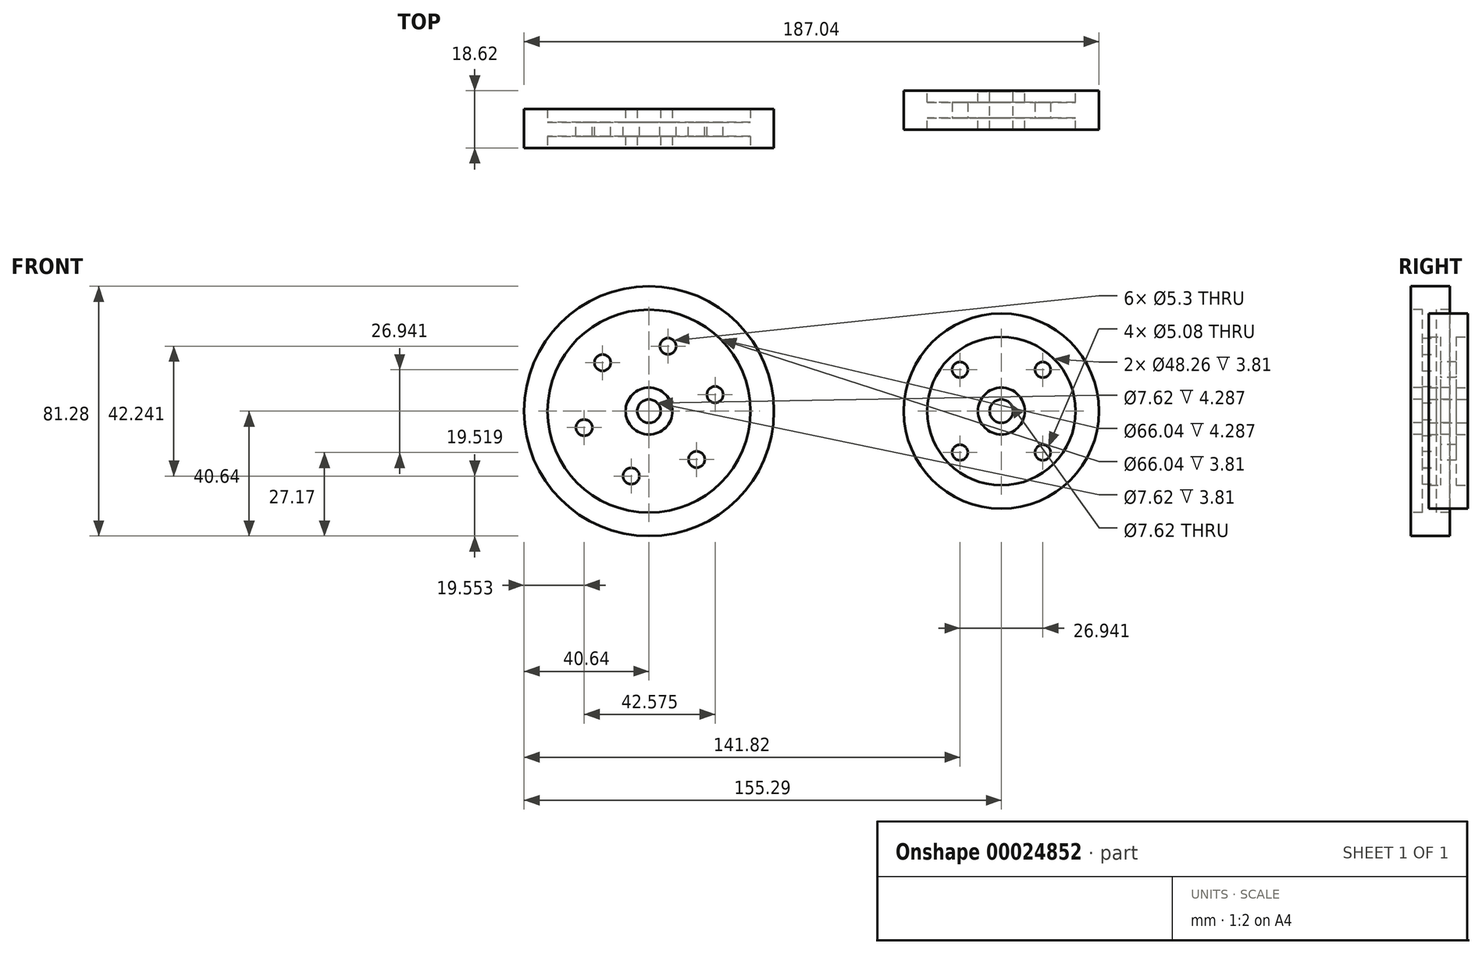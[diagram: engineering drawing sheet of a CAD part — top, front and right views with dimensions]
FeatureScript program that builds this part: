
annotation { "Feature Type Name" : "Feature", "Feature Type Description" : "" }
export const myFeature = defineFeature(function(context is Context, id is Id, definition is map)
    precondition{}
    {
        {
            var Q0;
            Q0=qCreatedBy(makeId("Top.planeOp"),FACE);
            var sketch = newSketch(context, id + "F0", { "sketchPlane" : qUnion([Q0])});
            skLineSegment(sketch, "E0", {"start": v(0, 3.81) * mm, "end": v(0, 27.58) * mm, "construction": true});
            skLineSegment(sketch, "E1", {"start": v(0, 27.58) * mm, "end": v(0, 12.7) * mm, "construction": true});
            skLineSegment(sketch, "E2.bottom", {"start": v(-24.13, 0) * mm, "end": v(-31.75, 0) * mm});
            skLineSegment(sketch, "E2.top", {"start": v(-24.13, 12.7) * mm, "end": v(-31.75, 12.7) * mm});
            skLineSegment(sketch, "E2.right", {"start": v(-31.75, 0) * mm, "end": v(-31.75, 12.7) * mm});
            skLineSegment(sketch, "E3.right", {"start": v(-24.13, 0) * mm, "end": v(-24.13, 3.8) * mm});
            skLineSegment(sketch, "E4.right", {"start": v(-24.13, 12.7) * mm, "end": v(-24.13, 8.9) * mm});
            skPoint(sketch, "E5.orphan", {"position": v(0, 12.7) * mm});
            skLineSegment(sketch, "E6.trimOffspring", {"start": v(0, 0) * mm, "end": v(0, -33.8) * mm, "construction": true});
            skLineSegment(sketch, "E7.bottom", {"start": v(-3.81, 0) * mm, "end": v(-7.62, 0) * mm});
            skLineSegment(sketch, "E7.top", {"start": v(-3.81, 12.48) * mm, "end": v(-7.62, 12.48) * mm});
            skLineSegment(sketch, "E7.left", {"start": v(-3.81, 0) * mm, "end": v(-3.81, 12.48) * mm});
            skLineSegment(sketch, "E7.right", {"start": v(-7.62, 0) * mm, "end": v(-7.62, 3.8) * mm});
            skLineSegment(sketch, "E8.trimOffspring", {"start": v(-7.62, 8.9) * mm, "end": v(-24.13, 8.9) * mm});
            skLineSegment(sketch, "E9.trimOffspring", {"start": v(-7.62, 3.8) * mm, "end": v(-24.13, 3.8) * mm});
            skPoint(sketch, "E4.top.start.orphan", {"position": v(0, 8.9) * mm});
            skLineSegment(sketch, "E10.trimOffspring", {"start": v(-7.62, 8.9) * mm, "end": v(-7.62, 12.48) * mm});
            skSolve(sketch);
        }
        {
            var Q0;
            Q0 = qSketchRegion(id + "F0", true);
            var Q1;
            Q1=sQuery(id+"F0.wireOp",EDGE,"E6.trimOffspring");
            revolve(context, id + "F1", {"entities" : qUnion([Q0]), "axis" : qUnion([Q1]), "revolveType" : RevolveType.FULL});
        }
        {
            var Q0;
            Q0=qCreatedBy(makeId("Front.planeOp"),FACE);
            var sketch = newSketch(context, id + "F2", { "sketchPlane" : qUnion([Q0])});
            skPoint(sketch, "E11.rect.middle", {"position": v(0, 0) * mm});
            skLineSegment(sketch, "E12", {"start": v(-17.06, 17.06) * mm, "end": v(17.06, -17.06) * mm, "construction": true});
            skLineSegment(sketch, "E13", {"start": v(17.06, 17.06) * mm, "end": v(-17.06, -17.06) * mm, "construction": true});
            skCircle(sketch, "E14", {"center": v(-13.47, 13.47) * mm, "radius": 2.54 * mm});
            skCircle(sketch, "E15", {"center": v(13.47, 13.47) * mm, "radius": 2.54 * mm});
            skCircle(sketch, "E16", {"center": v(-13.47, -13.47) * mm, "radius": 2.54 * mm});
            skCircle(sketch, "E17", {"center": v(13.47, -13.47) * mm, "radius": 2.54 * mm});
            skSolve(sketch);
        }
        {
            var Q0;
            Q0=makeQuery(id+"F2.imprint","IMPRINT",FACE,{"disambiguationData":[TD([[makeQuery(id+"F2.imprint","IMPRINT",EDGE,{"derivedFrom":sQuery(id+"F2.wireOp",EDGE,"E14")}),1.0]])]});
            var Q1;
            Q1=makeQuery(id+"F2.imprint","IMPRINT",FACE,{"disambiguationData":[TD([[makeQuery(id+"F2.imprint","IMPRINT",EDGE,{"derivedFrom":sQuery(id+"F2.wireOp",EDGE,"E15")}),1.0]])]});
            var Q2;
            Q2=makeQuery(id+"F2.imprint","IMPRINT",FACE,{"disambiguationData":[TD([[makeQuery(id+"F2.imprint","IMPRINT",EDGE,{"derivedFrom":sQuery(id+"F2.wireOp",EDGE,"E17")}),1.0]])]});
            var Q3;
            Q3=makeQuery(id+"F2.imprint","IMPRINT",FACE,{"disambiguationData":[TD([[makeQuery(id+"F2.imprint","IMPRINT",EDGE,{"derivedFrom":sQuery(id+"F2.wireOp",EDGE,"E16")}),1.0]])]});
            extrude(context, id + "F3", {"entities" : qUnion([Q0, Q1, Q2, Q3]), "operationType" : NewBodyOperationType.REMOVE, "oppositeDirection" : true, "depth" : 25.4 * mm});
        }
        {
            var Q0;
            Q0=qCreatedBy(makeId("Top.planeOp"),FACE);
            var sketch = newSketch(context, id + "F4", { "sketchPlane" : qUnion([Q0])});
            skLineSegment(sketch, "E18", {"start": v(-114.51, 26.7) * mm, "end": v(-114.51, -38.4) * mm, "construction": true});
            skLineSegment(sketch, "E19.bottom", {"start": v(-147.67, -5.92) * mm, "end": v(-155.29, -5.92) * mm});
            skLineSegment(sketch, "E19.top", {"start": v(-147.67, 6.78) * mm, "end": v(-155.29, 6.78) * mm});
            skLineSegment(sketch, "E19.left", {"start": v(-114.65, -5.92) * mm, "end": v(-114.65, 6.78) * mm});
            skLineSegment(sketch, "E19.right", {"start": v(-155.29, -5.92) * mm, "end": v(-155.29, 6.78) * mm});
            skLineSegment(sketch, "E20.top", {"start": v(-114.65, -2.1) * mm, "end": v(-118.46, -2.1) * mm});
            skLineSegment(sketch, "E20.left", {"start": v(-114.65, -5.92) * mm, "end": v(-114.65, -2.1) * mm});
            skLineSegment(sketch, "E20.right", {"start": v(-147.67, -5.92) * mm, "end": v(-147.67, -2.1) * mm});
            skLineSegment(sketch, "E21.top", {"start": v(-114.65, 2.5) * mm, "end": v(-118.46, 2.5) * mm});
            skLineSegment(sketch, "E21.left", {"start": v(-114.65, 6.78) * mm, "end": v(-114.65, 2.5) * mm});
            skLineSegment(sketch, "E21.right", {"start": v(-147.67, 6.78) * mm, "end": v(-147.67, 2.5) * mm});
            skLineSegment(sketch, "E22.bottom", {"start": v(-122.27, 6.78) * mm, "end": v(-118.46, 6.78) * mm});
            skLineSegment(sketch, "E22.top", {"start": v(-122.27, -5.92) * mm, "end": v(-118.46, -5.92) * mm});
            skLineSegment(sketch, "E22.left", {"start": v(-122.27, 6.78) * mm, "end": v(-122.27, 2.5) * mm});
            skLineSegment(sketch, "E22.right", {"start": v(-118.46, 6.78) * mm, "end": v(-118.46, 2.5) * mm});
            skLineSegment(sketch, "E23.trimOffspring", {"start": v(-122.27, 2.5) * mm, "end": v(-147.67, 2.5) * mm});
            skLineSegment(sketch, "E24.trimOffspring", {"start": v(-122.27, -2.1) * mm, "end": v(-147.67, -2.1) * mm});
            skLineSegment(sketch, "E25.trimOffspring", {"start": v(-118.46, -2.1) * mm, "end": v(-118.46, -5.92) * mm});
            skLineSegment(sketch, "E26.trimOffspring", {"start": v(-122.27, -2.1) * mm, "end": v(-122.27, -5.92) * mm});
            skSolve(sketch);
        }
        {
            var Q0;
            Q0 = qSketchRegion(id + "F4", true);
            var Q1;
            Q1=sQuery(id+"F4.wireOp",EDGE,"E19.left");
            revolve(context, id + "F5", {"entities" : qUnion([Q0]), "axis" : qUnion([Q1]), "revolveType" : RevolveType.FULL});
        }
        {
            var Q0;
            Q0=qCreatedBy(makeId("Front.planeOp"),FACE);
            var sketch = newSketch(context, id + "F6", { "sketchPlane" : qUnion([Q0])});
            skCircle(sketch, "E27", {"center": v(-129.74, 15.75) * mm, "radius": 2.65 * mm});
            skCircle(sketch, "E28.1.0", {"center": v(-135.74, -5.37) * mm, "radius": 2.65 * mm});
            skCircle(sketch, "E28.2.0", {"center": v(-120.44, -21.12) * mm, "radius": 2.65 * mm});
            skCircle(sketch, "E28.3.0", {"center": v(-99.16, -15.75) * mm, "radius": 2.65 * mm});
            skCircle(sketch, "E28.4.0", {"center": v(-93.16, 5.37) * mm, "radius": 2.65 * mm});
            skCircle(sketch, "E28.5.0", {"center": v(-108.46, 21.12) * mm, "radius": 2.65 * mm});
            skPoint(sketch, "E28.center", {"position": v(-114.45, 0) * mm});
            skSolve(sketch);
        }
        {
            var Q0;
            Q0 = qSketchRegion(id + "F6", true);
            extrude(context, id + "F7", {"entities" : qUnion([Q0]), "operationType" : NewBodyOperationType.REMOVE, "endBound" : BoundingType.THROUGH_ALL, "depth" : 70 * mm, "hasSecondDirection" : true, "secondDirectionOppositeDirection" : true, "secondDirectionDepth" : 25 * mm});
        }
    });
